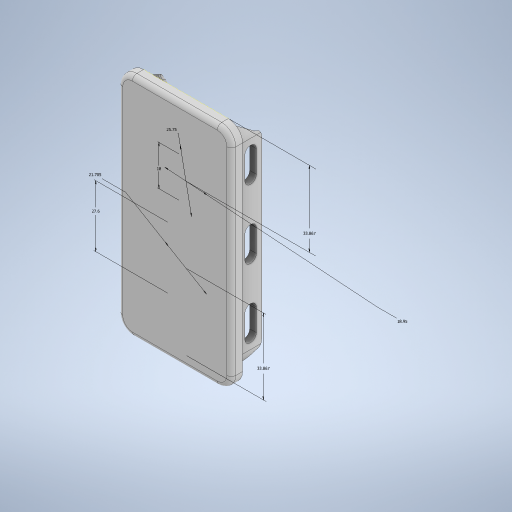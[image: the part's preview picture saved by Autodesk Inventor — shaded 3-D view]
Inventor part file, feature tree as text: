
AUTODESK INVENTOR PART (.ipt)
format: ipt  version: 2023 (Build 270158000, 158)  size: 591,872 bytes
history: native  units: mm
features: sketch x8, extrude x5, fillet x3, plane x2, mirror x1, chamfer x1
ambient origin geometry x8: Origin, YZ Plane, XZ Plane, XY Plane, X Axis, Y Axis, Z Axis, Center Point
bodies: Solid1 (feature_tree)
feature tree (20):
  extrude  "Extrusion1"  Depth=50.8mm
  fillet  "Fillet1"  Radius=6.35mm
  sketch  "Sketch3"  dims[d6=3.375mm d7=6.35mm]
  sketch  "Sketch2"  dims[d3=5.0mm d4=0.0mm d5=2.0mm]
  sketch  "Sketch4"  dims[d8=21.705mm d9=33.866667mm]
  extrude  "Extrusion2"  Depth=2.0mm
  sketch  "Sketch5"  dims[d10=33.866667mm d11=18.95mm]
  extrude  "Extrusion6"  Depth=6.35mm
  extrude  "Extrusion7"  Depth=33.866667mm
  extrude  "Extrusion8"  Depth=18.95mm
  plane  "Work Plane1"
  mirror  "Mirror1"
  chamfer  "Chamfer2"  Distance=12.0mm
  fillet  "Fillet2"  Radius=27.6mm
  fillet  "Fillet3"  Radius=25.75mm
  sketch  "Sketch1"  dims[d0=101.6mm d1=50.8mm d2=6.35mm]
  sketch  "Sketch6"  dims[d13=18.0mm]
  sketch  "Sketch7"  dims[d14=3.0mm]
  sketch  "Sketch8"  dims[d15=3.0mm d16=12.0mm d17=0.0mm d20=27.6mm d23=25.75mm d29=2.613mm d30=7.0mm d31=2.613mm d32=20.0mm d33=20.0mm d34=2.613mm d35=10.0mm d36=0.0mm d37=0.0mm d38=2.613mm d39=10.0mm d40=7.0mm d41=0.0mm d42=0.0mm d43=1.0mm d44=0.0mm d45=2.0mm d46=2.0mm d47=2.5mm d48=2.0mm d49=45.0deg]
  plane  "Work Plane2"
